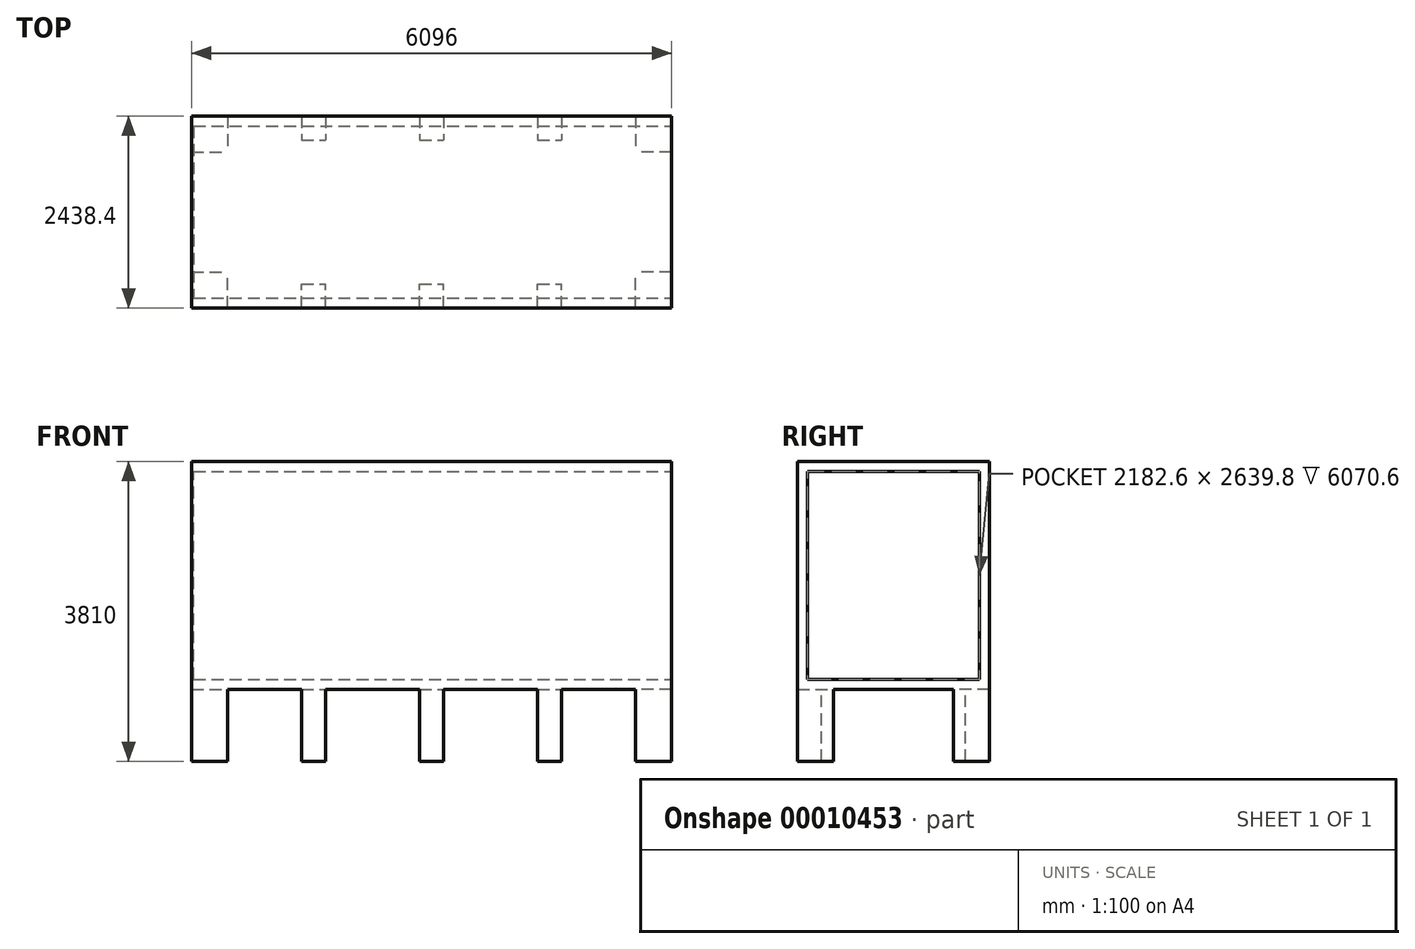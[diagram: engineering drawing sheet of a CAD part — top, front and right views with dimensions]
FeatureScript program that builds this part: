
annotation { "Feature Type Name" : "Feature", "Feature Type Description" : "" }
export const myFeature = defineFeature(function(context is Context, id is Id, definition is map)
    precondition{}
    {
        {
            var Q0;
            Q0=qCreatedBy(makeId("Right.planeOp"),FACE);
            var sketch = newSketch(context, id + "F0", { "sketchPlane" : qUnion([Q0])});
            skLineSegment(sketch, "E0.bottom", {"start": v(-1207.03, 2895.6) * mm, "end": v(1231.37, 2895.6) * mm});
            skLineSegment(sketch, "E0.top", {"start": v(-1207.03, 0) * mm, "end": v(1231.37, 0) * mm});
            skLineSegment(sketch, "E0.left", {"start": v(-1207.03, 2895.6) * mm, "end": v(-1207.03, 0) * mm});
            skLineSegment(sketch, "E0.right", {"start": v(1231.37, 2895.6) * mm, "end": v(1231.37, 0) * mm});
            skSolve(sketch);
        }
        {
            var Q0;
            Q0 = qSketchRegion(id + "F0", true);
            extrude(context, id + "F1", {"entities" : qUnion([Q0]), "depth" : 6096 * mm});
        }
        {
            var Q0;
            Q0=makeQuery(id+"F1.opExtrude","CAP_FACE",FACE,{"disambiguationData":[OSD([sQuery(id+"F0.wireOp",EDGE,"E0.bottom"),sQuery(id+"F0.wireOp",EDGE,"E0.top"),sQuery(id+"F0.wireOp",EDGE,"E0.left"),sQuery(id+"F0.wireOp",EDGE,"E0.right")])],"isStart":false});
            var sketch = newSketch(context, id + "F2", { "sketchPlane" : qUnion([Q0])});
            skLineSegment(sketch, "E1.0", {"start": v(1103.47, 2767.7) * mm, "end": v(-1079.13, 2767.7) * mm});
            skLineSegment(sketch, "E1.1", {"start": v(1103.47, 127.9) * mm, "end": v(1103.47, 2767.7) * mm});
            skLineSegment(sketch, "E1.2", {"start": v(-1079.13, 127.9) * mm, "end": v(1103.47, 127.9) * mm});
            skLineSegment(sketch, "E1.3", {"start": v(-1079.13, 2767.7) * mm, "end": v(-1079.13, 127.9) * mm});
            skSolve(sketch);
        }
        {
            var Q0;
            Q0 = qSketchRegion(id + "F2", true);
            extrude(context, id + "F3", {"entities" : qUnion([Q0]), "operationType" : NewBodyOperationType.REMOVE, "oppositeDirection" : true, "depth" : 6070.6 * mm});
        }
        {
            var Q0;
            Q0=makeQuery(id+"F1.opExtrude","SWEPT_FACE",FACE,{"disambiguationData":[OSD([sQuery(id+"F0.wireOp",EDGE,"E0.top")])]});
            var sketch = newSketch(context, id + "F4", { "sketchPlane" : qUnion([Q0])});
            skLineSegment(sketch, "E2.bottom", {"start": v(0, 1207.03) * mm, "end": v(457.2, 1207.03) * mm});
            skLineSegment(sketch, "E2.top", {"start": v(0, 749.83) * mm, "end": v(457.2, 749.83) * mm});
            skLineSegment(sketch, "E2.left", {"start": v(0, 1207.03) * mm, "end": v(0, 749.83) * mm});
            skLineSegment(sketch, "E2.right", {"start": v(457.2, 1207.03) * mm, "end": v(457.2, 749.83) * mm});
            skLineSegment(sketch, "E3.bottom", {"start": v(0, -1231.37) * mm, "end": v(457.2, -1231.37) * mm});
            skLineSegment(sketch, "E3.top", {"start": v(0, -774.17) * mm, "end": v(457.2, -774.17) * mm});
            skLineSegment(sketch, "E3.left", {"start": v(0, -1231.37) * mm, "end": v(0, -774.17) * mm});
            skLineSegment(sketch, "E3.right", {"start": v(457.2, -1231.37) * mm, "end": v(457.2, -774.17) * mm});
            skLineSegment(sketch, "E4.bottom", {"start": v(6096, -1231.37) * mm, "end": v(5638.8, -1231.37) * mm});
            skLineSegment(sketch, "E4.top", {"start": v(6096, -774.17) * mm, "end": v(5638.8, -774.17) * mm});
            skLineSegment(sketch, "E4.left", {"start": v(6096, -1231.37) * mm, "end": v(6096, -774.17) * mm});
            skLineSegment(sketch, "E4.right", {"start": v(5638.8, -1231.37) * mm, "end": v(5638.8, -774.17) * mm});
            skLineSegment(sketch, "E5.bottom", {"start": v(6096, 1207.03) * mm, "end": v(5638.8, 1207.03) * mm});
            skLineSegment(sketch, "E5.top", {"start": v(6096, 749.83) * mm, "end": v(5638.8, 749.83) * mm});
            skLineSegment(sketch, "E5.left", {"start": v(6096, 1207.03) * mm, "end": v(6096, 749.83) * mm});
            skLineSegment(sketch, "E5.right", {"start": v(5638.8, 1207.03) * mm, "end": v(5638.8, 749.83) * mm});
            skLineSegment(sketch, "E6.bottom", {"start": v(1397, 1207.03) * mm, "end": v(1701.8, 1207.03) * mm});
            skLineSegment(sketch, "E6.top", {"start": v(1397, 902.23) * mm, "end": v(1701.8, 902.23) * mm});
            skLineSegment(sketch, "E6.left", {"start": v(1397, 1207.03) * mm, "end": v(1397, 902.23) * mm});
            skLineSegment(sketch, "E6.right", {"start": v(1701.8, 1207.03) * mm, "end": v(1701.8, 902.23) * mm});
            skLineSegment(sketch, "E7.bottom", {"start": v(1397, -1231.37) * mm, "end": v(1701.8, -1231.37) * mm});
            skLineSegment(sketch, "E7.top", {"start": v(1397, -926.57) * mm, "end": v(1701.8, -926.57) * mm});
            skLineSegment(sketch, "E7.left", {"start": v(1397, -1231.37) * mm, "end": v(1397, -926.57) * mm});
            skLineSegment(sketch, "E7.right", {"start": v(1701.8, -1231.37) * mm, "end": v(1701.8, -926.57) * mm});
            skLineSegment(sketch, "E8.bottom", {"start": v(2895.6, 1207.03) * mm, "end": v(3200.4, 1207.03) * mm});
            skLineSegment(sketch, "E8.top", {"start": v(2895.6, 902.23) * mm, "end": v(3200.4, 902.23) * mm});
            skLineSegment(sketch, "E8.left", {"start": v(2895.6, 1207.03) * mm, "end": v(2895.6, 902.23) * mm});
            skLineSegment(sketch, "E8.right", {"start": v(3200.4, 1207.03) * mm, "end": v(3200.4, 902.23) * mm});
            skLineSegment(sketch, "E9.bottom", {"start": v(2895.6, -1231.37) * mm, "end": v(3200.4, -1231.37) * mm});
            skLineSegment(sketch, "E9.top", {"start": v(2895.6, -926.57) * mm, "end": v(3200.4, -926.57) * mm});
            skLineSegment(sketch, "E9.left", {"start": v(2895.6, -1231.37) * mm, "end": v(2895.6, -926.57) * mm});
            skLineSegment(sketch, "E9.right", {"start": v(3200.4, -1231.37) * mm, "end": v(3200.4, -926.57) * mm});
            skLineSegment(sketch, "E10.bottom", {"start": v(4394.2, -1231.37) * mm, "end": v(4699, -1231.37) * mm});
            skLineSegment(sketch, "E10.top", {"start": v(4394.2, -926.57) * mm, "end": v(4699, -926.57) * mm});
            skLineSegment(sketch, "E10.left", {"start": v(4394.2, -1231.37) * mm, "end": v(4394.2, -926.57) * mm});
            skLineSegment(sketch, "E10.right", {"start": v(4699, -1231.37) * mm, "end": v(4699, -926.57) * mm});
            skLineSegment(sketch, "E11.bottom", {"start": v(4394.2, 1207.03) * mm, "end": v(4699, 1207.03) * mm});
            skLineSegment(sketch, "E11.top", {"start": v(4394.2, 902.23) * mm, "end": v(4699, 902.23) * mm});
            skLineSegment(sketch, "E11.left", {"start": v(4394.2, 1207.03) * mm, "end": v(4394.2, 902.23) * mm});
            skLineSegment(sketch, "E11.right", {"start": v(4699, 1207.03) * mm, "end": v(4699, 902.23) * mm});
            skSolve(sketch);
        }
        {
            var Q0;
            Q0 = qSketchRegion(id + "F4", true);
            extrude(context, id + "F5", {"entities" : qUnion([Q0]), "operationType" : NewBodyOperationType.ADD, "depth" : 914.4 * mm});
        }
    });
